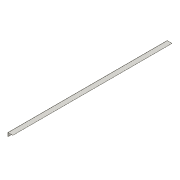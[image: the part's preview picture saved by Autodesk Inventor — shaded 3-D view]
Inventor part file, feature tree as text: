
AUTODESK INVENTOR PART (.ipt)
format: ipt  version: 2018 (Build 220112000, 112)  size: 85,504 bytes
history: native  units: in
note: dims shown in document units (in); Inventor stores cm internally (conversion verified against a paired STEP export)
features: extrude x2, sketch x2
ambient origin geometry x8: Origin, YZ Plane, XZ Plane, XY Plane, X Axis, Y Axis, Z Axis, Center Point
bodies: Solid1 (feature_tree)
feature tree (4):
  extrude  "Extrusion1"  Depth=3.0in
  extrude  "Extrusion2"  Depth=0.0747in
  sketch  "Sketch1"  dims[d0=4.0in d1=3.0in]
  sketch  "Sketch2"  dims[d2=0.0747in d3=0.0747in d4=131.0in d5=0.0in d6=15.0deg d7=1.0in d8=0.0in]
